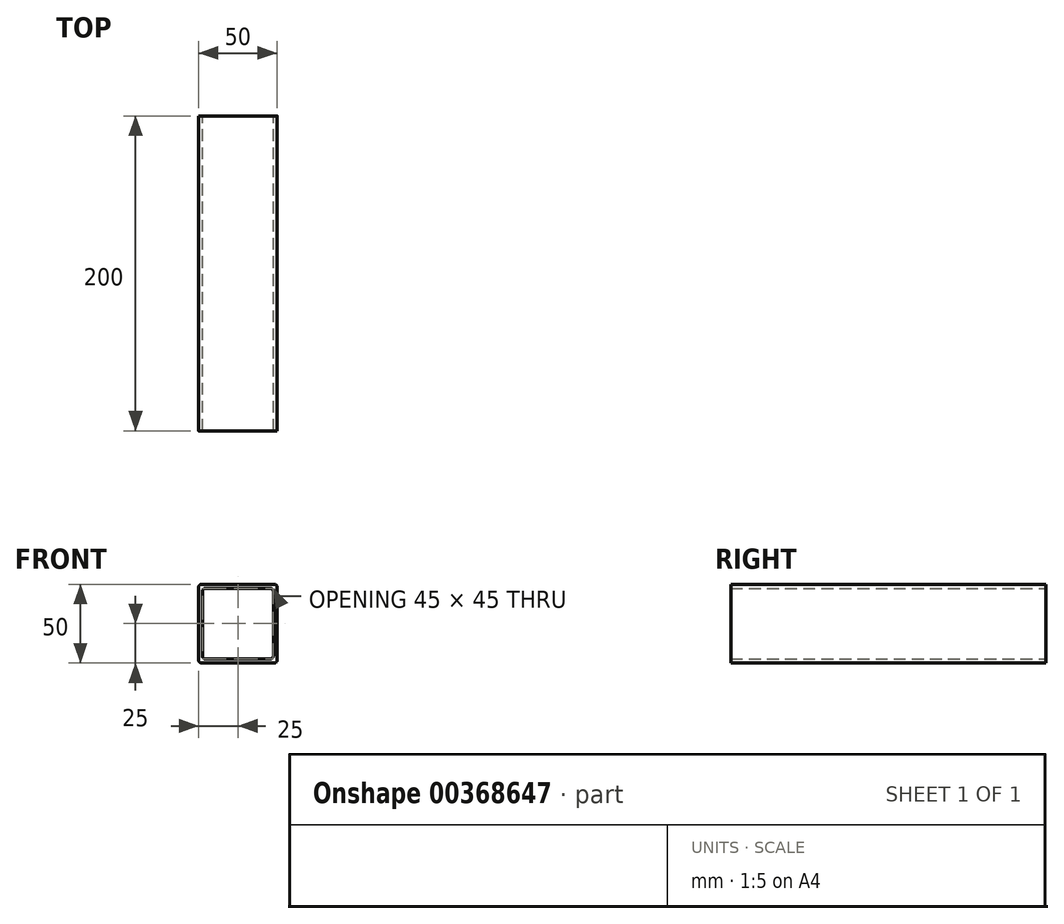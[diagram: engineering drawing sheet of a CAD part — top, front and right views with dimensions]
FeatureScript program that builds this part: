
annotation { "Feature Type Name" : "Feature", "Feature Type Description" : "" }
export const myFeature = defineFeature(function(context is Context, id is Id, definition is map)
    precondition{}
    {
        {
            var Q0;
            Q0=qCreatedBy(makeId("Front.planeOp"),FACE);
            var sketch = newSketch(context, id + "F0", { "sketchPlane" : qUnion([Q0])});
            skLineSegment(sketch, "E0.bottom", {"start": v(23, 25) * mm, "end": v(-23, 25) * mm});
            skLineSegment(sketch, "E0.top", {"start": v(23, -25) * mm, "end": v(-23, -25) * mm});
            skLineSegment(sketch, "E0.left", {"start": v(25, 23) * mm, "end": v(25, -23) * mm});
            skLineSegment(sketch, "E0.right", {"start": v(-25, 23) * mm, "end": v(-25, -23) * mm});
            skPoint(sketch, "E0.middle", {"position": v(0, 0) * mm});
            skLineSegment(sketch, "E1.bottom", {"start": v(20.5, 22.5) * mm, "end": v(-20.5, 22.5) * mm});
            skLineSegment(sketch, "E1.top", {"start": v(20.5, -22.5) * mm, "end": v(-20.5, -22.5) * mm});
            skLineSegment(sketch, "E1.left", {"start": v(22.5, 20.5) * mm, "end": v(22.5, -20.5) * mm});
            skLineSegment(sketch, "E1.right", {"start": v(-22.5, 20.5) * mm, "end": v(-22.5, -20.5) * mm});
            skPoint(sketch, "E2.visualSharp", {"position": v(-25, 25) * mm});
            skArc(sketch, "E2.filletArc", {"start": v(-23, 25) * mm, "mid": v(-24.41, 24.41) * mm, "end": v(-25, 23) * mm});
            skPoint(sketch, "E3.visualSharp", {"position": v(25, 25) * mm});
            skArc(sketch, "E3.filletArc", {"start": v(25, 23) * mm, "mid": v(24.41, 24.41) * mm, "end": v(23, 25) * mm});
            skPoint(sketch, "E4.visualSharp", {"position": v(22.5, 22.5) * mm});
            skArc(sketch, "E4.filletArc", {"start": v(22.5, 20.5) * mm, "mid": v(21.91, 21.91) * mm, "end": v(20.5, 22.5) * mm});
            skPoint(sketch, "E5.visualSharp", {"position": v(-22.5, 22.5) * mm});
            skArc(sketch, "E5.filletArc", {"start": v(-20.5, 22.5) * mm, "mid": v(-21.91, 21.91) * mm, "end": v(-22.5, 20.5) * mm});
            skPoint(sketch, "E6.visualSharp", {"position": v(-22.5, -22.5) * mm});
            skArc(sketch, "E6.filletArc", {"start": v(-22.5, -20.5) * mm, "mid": v(-21.91, -21.91) * mm, "end": v(-20.5, -22.5) * mm});
            skPoint(sketch, "E7.visualSharp", {"position": v(-25, -25) * mm});
            skArc(sketch, "E7.filletArc", {"start": v(-25, -23) * mm, "mid": v(-24.41, -24.41) * mm, "end": v(-23, -25) * mm});
            skPoint(sketch, "E8.visualSharp", {"position": v(22.5, -22.5) * mm});
            skArc(sketch, "E8.filletArc", {"start": v(20.5, -22.5) * mm, "mid": v(21.91, -21.91) * mm, "end": v(22.5, -20.5) * mm});
            skPoint(sketch, "E9.visualSharp", {"position": v(25, -25) * mm});
            skArc(sketch, "E9.filletArc", {"start": v(23, -25) * mm, "mid": v(24.41, -24.41) * mm, "end": v(25, -23) * mm});
            skSolve(sketch);
        }
        {
            var Q0;
            Q0=qSketchRegion(id+"F0",true);
            extrude(context, id + "F1", {"entities" : qUnion([Q0]), "endBound" : BoundingType.SYMMETRIC, "depth" : 200 * mm});
        }
    });
